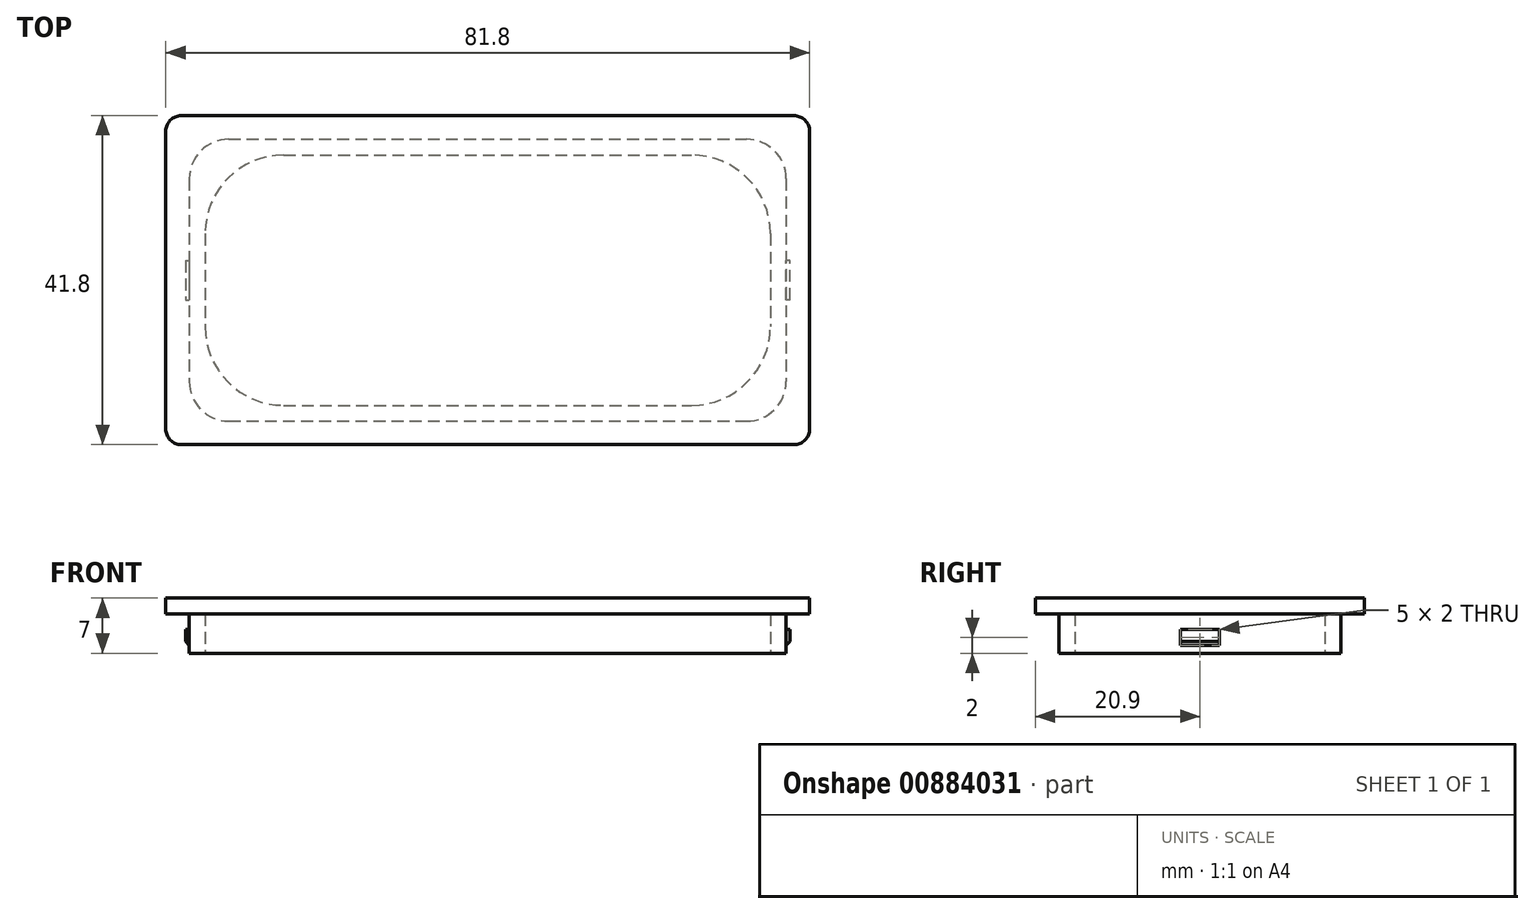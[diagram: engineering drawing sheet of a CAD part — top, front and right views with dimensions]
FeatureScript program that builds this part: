
annotation { "Feature Type Name" : "Feature", "Feature Type Description" : "" }
export const myFeature = defineFeature(function(context is Context, id is Id, definition is map)
    precondition{}
    {
        {
            var Q0;
            Q0=qCreatedBy(makeId("Top.planeOp"),FACE);
            var sketch = newSketch(context, id + "F0", { "sketchPlane" : qUnion([Q0])});
            skLineSegment(sketch, "E0.bottom", {"start": v(-41.8, 20.29) * mm, "end": v(34, 20.29) * mm});
            skLineSegment(sketch, "E0.top", {"start": v(-41.8, -15.51) * mm, "end": v(34, -15.51) * mm});
            skLineSegment(sketch, "E0.left", {"start": v(-41.8, 20.29) * mm, "end": v(-41.8, -15.51) * mm});
            skLineSegment(sketch, "E0.right", {"start": v(34, 20.29) * mm, "end": v(34, -15.51) * mm});
            skLineSegment(sketch, "E1.bottom", {"start": v(-39.8, 18.29) * mm, "end": v(32, 18.29) * mm});
            skLineSegment(sketch, "E1.top", {"start": v(-39.8, -13.51) * mm, "end": v(32, -13.51) * mm});
            skLineSegment(sketch, "E1.left", {"start": v(-39.8, 18.29) * mm, "end": v(-39.8, -13.51) * mm});
            skLineSegment(sketch, "E1.right", {"start": v(32, 18.29) * mm, "end": v(32, -13.51) * mm});
            skLineSegment(sketch, "E2", {"start": v(-39.8, 2.39) * mm, "end": v(32, 2.39) * mm, "construction": true});
            skLineSegment(sketch, "E3", {"start": v(-3.9, 20.29) * mm, "end": v(-3.9, -15.51) * mm, "construction": true});
            skPoint(sketch, "E4", {"position": v(-3.9, 2.39) * mm});
            skLineSegment(sketch, "E5", {"start": v(-39.8, 10.47) * mm, "end": v(-41.8, 10.47) * mm, "construction": true});
            skLineSegment(sketch, "E6", {"start": v(-20.1, 20.29) * mm, "end": v(-20.1, 18.29) * mm, "construction": true});
            skSolve(sketch);
        }
        {
            var Q0;
            Q0=makeQuery(id+"F0.imprint","IMPRINT",FACE,{"disambiguationData":[TD([[makeQuery(id+"F0.imprint","IMPRINT",EDGE,{"derivedFrom":sQuery(id+"F0.wireOp",EDGE,"E0.bottom")}),-1.0]])]});
            extrude(context, id + "F1", {"entities" : qUnion([Q0]), "depth" : 5 * mm, "offsetDistance" : 25 * mm});
        }
        {
            var Q0;
            Q0=makeQuery(id+"F1.opExtrude","CAP_FACE",FACE,{"disambiguationData":[OSD([sQuery(id+"F0.wireOp",EDGE,"E0.bottom"),sQuery(id+"F0.wireOp",EDGE,"E0.top"),sQuery(id+"F0.wireOp",EDGE,"E0.left"),sQuery(id+"F0.wireOp",EDGE,"E0.right"),sQuery(id+"F0.wireOp",EDGE,"E1.bottom"),sQuery(id+"F0.wireOp",EDGE,"E1.top"),sQuery(id+"F0.wireOp",EDGE,"E1.left"),sQuery(id+"F0.wireOp",EDGE,"E1.right")])],"isStart":false});
            var sketch = newSketch(context, id + "F2", { "sketchPlane" : qUnion([Q0])});
            skLineSegment(sketch, "E7.bottom", {"start": v(-44.8, 23.29) * mm, "end": v(37, 23.29) * mm});
            skLineSegment(sketch, "E7.top", {"start": v(-44.8, -18.51) * mm, "end": v(37, -18.51) * mm});
            skLineSegment(sketch, "E7.left", {"start": v(-44.8, 23.29) * mm, "end": v(-44.8, -18.51) * mm});
            skLineSegment(sketch, "E7.right", {"start": v(37, 23.29) * mm, "end": v(37, -18.51) * mm});
            skLineSegment(sketch, "E8", {"start": v(-41.8, 20.29) * mm, "end": v(-44.8, 20.29) * mm, "construction": true});
            skLineSegment(sketch, "E9", {"start": v(-41.8, 20.29) * mm, "end": v(-41.8, 23.29) * mm, "construction": true});
            skLineSegment(sketch, "E10", {"start": v(34, -15.51) * mm, "end": v(34, -18.51) * mm});
            skLineSegment(sketch, "E11", {"start": v(34, -15.51) * mm, "end": v(37, -15.51) * mm});
            skSolve(sketch);
        }
        {
            var Q0;
            Q0 = qSketchRegion(id + "F2", true);
            extrude(context, id + "F3", {"entities" : qUnion([Q0]), "operationType" : NewBodyOperationType.ADD, "depth" : 2 * mm, "offsetDistance" : 25 * mm});
        }
        {
            var Q0;
            Q0=makeQuery(id+"F1.opExtrude","SWEPT_EDGE",EDGE,{"disambiguationData":[OSD([sQuery(id+"F0.wireOp",EDGE,"E0.bottom"),sQuery(id+"F0.wireOp",EDGE,"E0.right")])]});
            var Q1;
            Q1=makeQuery(id+"F1.opExtrude","SWEPT_EDGE",EDGE,{"disambiguationData":[OSD([sQuery(id+"F0.wireOp",EDGE,"E0.top"),sQuery(id+"F0.wireOp",EDGE,"E0.right")])]});
            var Q2;
            Q2=makeQuery(id+"F1.opExtrude","SWEPT_EDGE",EDGE,{"disambiguationData":[OSD([sQuery(id+"F0.wireOp",EDGE,"E0.top"),sQuery(id+"F0.wireOp",EDGE,"E0.left")])]});
            var Q3;
            Q3=makeQuery(id+"F1.opExtrude","SWEPT_EDGE",EDGE,{"disambiguationData":[OSD([sQuery(id+"F0.wireOp",EDGE,"E0.bottom"),sQuery(id+"F0.wireOp",EDGE,"E0.left")])]});
            fillet(context, id + "F4", {"entities" : qUnion([Q0, Q1, Q2, Q3]), "radius" : 5 * mm, "tangentPropagation" : true, "allowEdgeOverflow" : false});
        }
        {
            var Q0;
            Q0=makeQuery(id+"F1.opExtrude","SWEPT_EDGE",EDGE,{"disambiguationData":[OSD([sQuery(id+"F0.wireOp",EDGE,"E1.top"),sQuery(id+"F0.wireOp",EDGE,"E1.right")])]});
            var Q1;
            Q1=makeQuery(id+"F1.opExtrude","SWEPT_EDGE",EDGE,{"disambiguationData":[OSD([sQuery(id+"F0.wireOp",EDGE,"E1.bottom"),sQuery(id+"F0.wireOp",EDGE,"E1.right")])]});
            var Q2;
            Q2=makeQuery(id+"F1.opExtrude","SWEPT_EDGE",EDGE,{"disambiguationData":[OSD([sQuery(id+"F0.wireOp",EDGE,"E1.bottom"),sQuery(id+"F0.wireOp",EDGE,"E1.left")])]});
            var Q3;
            Q3=makeQuery(id+"F1.opExtrude","SWEPT_EDGE",EDGE,{"disambiguationData":[OSD([sQuery(id+"F0.wireOp",EDGE,"E1.top"),sQuery(id+"F0.wireOp",EDGE,"E1.left")])]});
            fillet(context, id + "F5", {"entities" : qUnion([Q0, Q1, Q2, Q3]), "radius" : 10 * mm, "tangentPropagation" : true, "allowEdgeOverflow" : false});
        }
        {
            var Q0;
            Q0=makeQuery(id+"F3.opExtrude","SWEPT_EDGE",EDGE,{"disambiguationData":[OSD([sQuery(id+"F2.wireOp",EDGE,"E7.top"),sQuery(id+"F2.wireOp",EDGE,"E7.right")])]});
            var Q1;
            Q1=makeQuery(id+"F3.opExtrude","SWEPT_EDGE",EDGE,{"disambiguationData":[OSD([sQuery(id+"F2.wireOp",EDGE,"E7.bottom"),sQuery(id+"F2.wireOp",EDGE,"E7.right")])]});
            var Q2;
            Q2=makeQuery(id+"F3.opExtrude","SWEPT_EDGE",EDGE,{"disambiguationData":[OSD([sQuery(id+"F2.wireOp",EDGE,"E7.bottom"),sQuery(id+"F2.wireOp",EDGE,"E7.left")])]});
            var Q3;
            Q3=makeQuery(id+"F3.opExtrude","SWEPT_EDGE",EDGE,{"disambiguationData":[OSD([sQuery(id+"F2.wireOp",EDGE,"E7.top"),sQuery(id+"F2.wireOp",EDGE,"E7.left")])]});
            fillet(context, id + "F6", {"entities" : qUnion([Q0, Q1, Q2, Q3]), "radius" : 2 * mm, "tangentPropagation" : true, "allowEdgeOverflow" : false});
        }
        {
            var Q0;
            Q0=makeQuery(id+"F1.opExtrude","SWEPT_FACE",FACE,{"disambiguationData":[OSD([sQuery(id+"F0.wireOp",EDGE,"E0.left")])]});
            var sketch = newSketch(context, id + "F7", { "sketchPlane" : qUnion([Q0])});
            skLineSegment(sketch, "E12.bottom", {"start": v(-4.89, 3) * mm, "end": v(0.11, 3) * mm});
            skLineSegment(sketch, "E12.top", {"start": v(-4.89, 1) * mm, "end": v(0.11, 1) * mm});
            skLineSegment(sketch, "E12.left", {"start": v(-4.89, 3) * mm, "end": v(-4.89, 1) * mm});
            skLineSegment(sketch, "E12.right", {"start": v(0.11, 3) * mm, "end": v(0.11, 1) * mm});
            skLineSegment(sketch, "E13", {"start": v(-2.39, 5) * mm, "end": v(-2.39, 3) * mm, "construction": true});
            skSolve(sketch);
        }
        {
            var Q0;
            Q0=makeQuery(id+"F7.imprint","IMPRINT",FACE,{"disambiguationData":[TD([[makeQuery(id+"F7.imprint","IMPRINT",EDGE,{"derivedFrom":sQuery(id+"F7.wireOp",EDGE,"E12.bottom")}),-1.0]])]});
            extrude(context, id + "F8", {"entities" : qUnion([Q0]), "operationType" : NewBodyOperationType.ADD, "depth" : 0.5 * mm, "offsetDistance" : 25 * mm});
        }
        {
            var Q0;
            Q0=makeQuery(id+"F1.opExtrude","SWEPT_FACE",FACE,{"disambiguationData":[OSD([sQuery(id+"F0.wireOp",EDGE,"E0.right")])]});
            var sketch = newSketch(context, id + "F9", { "sketchPlane" : qUnion([Q0])});
            skLineSegment(sketch, "E14.bottom", {"start": v(-0.11, 3) * mm, "end": v(4.89, 3) * mm});
            skLineSegment(sketch, "E14.top", {"start": v(-0.11, 1) * mm, "end": v(4.89, 1) * mm});
            skLineSegment(sketch, "E14.left", {"start": v(-0.11, 3) * mm, "end": v(-0.11, 1) * mm});
            skLineSegment(sketch, "E14.right", {"start": v(4.89, 3) * mm, "end": v(4.89, 1) * mm});
            skLineSegment(sketch, "E15", {"start": v(2.39, 5) * mm, "end": v(2.39, 3) * mm, "construction": true});
            skSolve(sketch);
        }
        {
            var Q0;
            Q0 = qSketchRegion(id + "F9", true);
            extrude(context, id + "F10", {"entities" : qUnion([Q0]), "operationType" : NewBodyOperationType.ADD, "depth" : 0.5 * mm, "offsetDistance" : 25 * mm});
        }
        {
            var Q0;
            Q0=makeQuery(id+"F10.opExtrude","CAP_EDGE",EDGE,{"disambiguationData":[OSD([sQuery(id+"F9.wireOp",EDGE,"E14.top")])],"isStart":false});
            var Q1;
            Q1=makeQuery(id+"F8.opExtrude","CAP_EDGE",EDGE,{"disambiguationData":[OSD([sQuery(id+"F7.wireOp",EDGE,"E12.top")])],"isStart":false});
            chamfer(context, id + "F11", {"entities" : qUnion([Q0, Q1]), "width" : 0.5 * mm, "tangentPropagation" : true});
        }
    });
